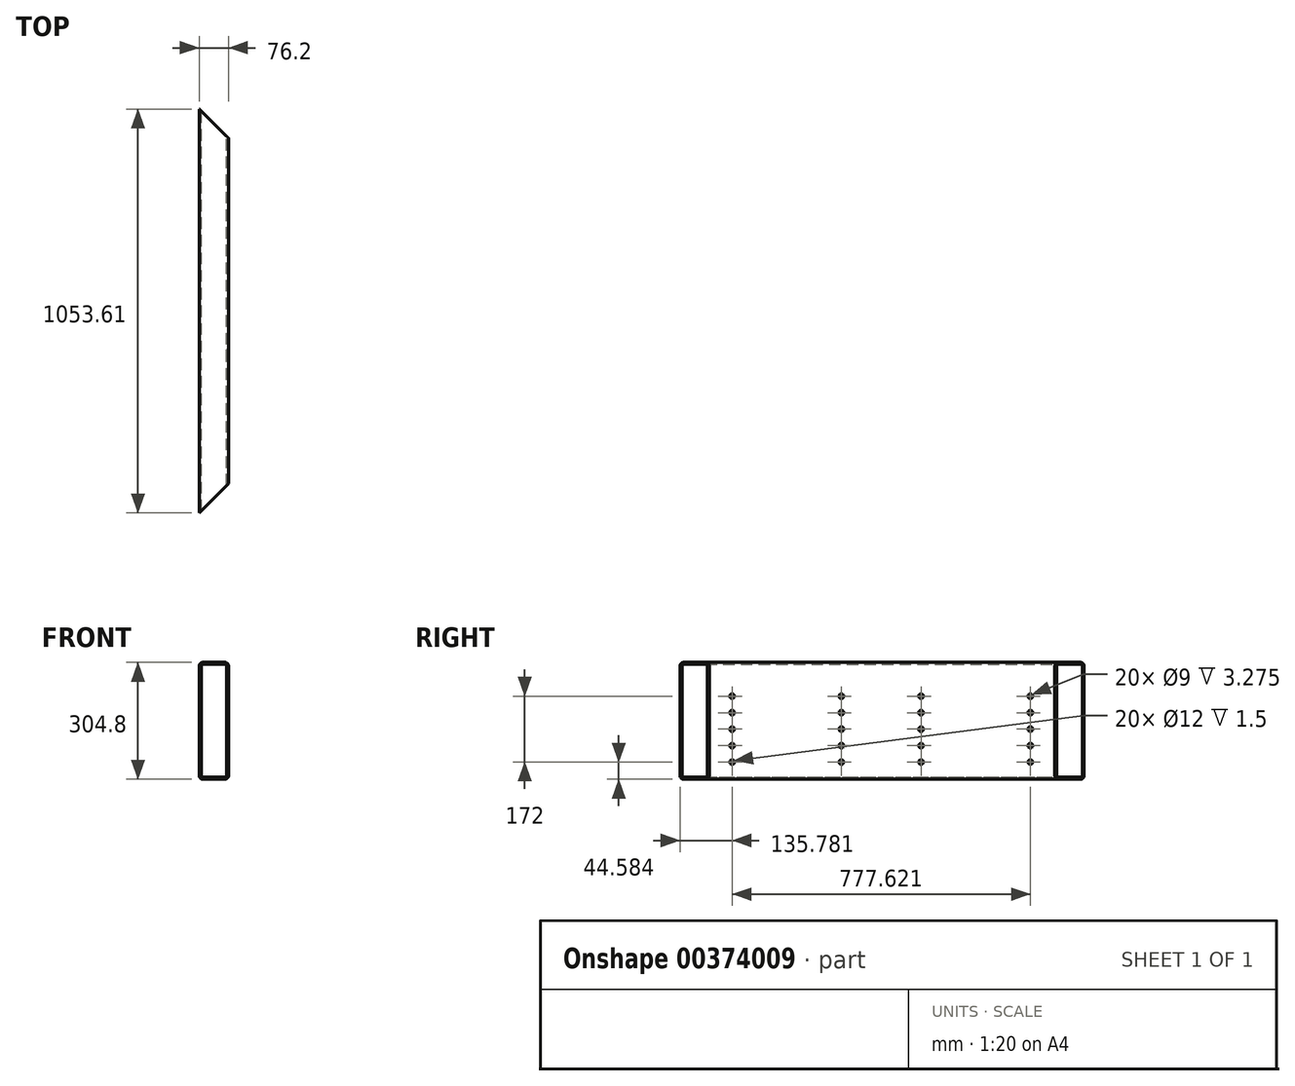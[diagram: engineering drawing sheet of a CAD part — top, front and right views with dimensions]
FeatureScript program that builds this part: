
annotation { "Feature Type Name" : "Feature", "Feature Type Description" : "" }
export const myFeature = defineFeature(function(context is Context, id is Id, definition is map)
    precondition{}
    {
        {
            var Q0;
            Q0=qCreatedBy(makeId("Front.planeOp"),FACE);
            var sketch = newSketch(context, id + "F0", { "sketchPlane" : qUnion([Q0])});
            skLineSegment(sketch, "E0.bottom", {"start": v(-9.55, -50.8) * mm, "end": v(-66.65, -50.8) * mm});
            skLineSegment(sketch, "E0.top", {"start": v(-9.55, 254) * mm, "end": v(-66.65, 254) * mm});
            skLineSegment(sketch, "E0.left", {"start": v(0, -41.25) * mm, "end": v(0, 244.45) * mm});
            skLineSegment(sketch, "E0.right", {"start": v(-76.2, -41.25) * mm, "end": v(-76.2, 244.45) * mm});
            skLineSegment(sketch, "E1.bottom", {"start": v(-66.65, 249.22) * mm, "end": v(-9.55, 249.22) * mm});
            skLineSegment(sketch, "E1.top", {"start": v(-66.65, -46.02) * mm, "end": v(-9.55, -46.02) * mm});
            skLineSegment(sketch, "E1.left", {"start": v(-71.42, 244.45) * mm, "end": v(-71.42, -41.25) * mm});
            skLineSegment(sketch, "E1.right", {"start": v(-4.78, 244.45) * mm, "end": v(-4.78, -41.25) * mm});
            skPoint(sketch, "E2.visualSharp", {"position": v(-71.42, 249.22) * mm});
            skArc(sketch, "E2.filletArc", {"start": v(-66.65, 249.22) * mm, "mid": v(-70.03, 247.83) * mm, "end": v(-71.42, 244.45) * mm});
            skPoint(sketch, "E3.visualSharp", {"position": v(-4.78, 249.22) * mm});
            skArc(sketch, "E3.filletArc", {"start": v(-4.78, 244.45) * mm, "mid": v(-6.17, 247.83) * mm, "end": v(-9.55, 249.22) * mm});
            skPoint(sketch, "E4.visualSharp", {"position": v(-4.78, -46.02) * mm});
            skArc(sketch, "E4.filletArc", {"start": v(-9.55, -46.02) * mm, "mid": v(-6.17, -44.63) * mm, "end": v(-4.78, -41.25) * mm});
            skPoint(sketch, "E5.visualSharp", {"position": v(-71.42, -46.02) * mm});
            skArc(sketch, "E5.filletArc", {"start": v(-71.42, -41.25) * mm, "mid": v(-70.03, -44.63) * mm, "end": v(-66.65, -46.02) * mm});
            skPoint(sketch, "E6.visualSharp", {"position": v(-76.2, 254) * mm});
            skArc(sketch, "E6.filletArc", {"start": v(-66.65, 254) * mm, "mid": v(-73.4, 251.2) * mm, "end": v(-76.2, 244.45) * mm});
            skPoint(sketch, "E7.visualSharp", {"position": v(0, 254) * mm});
            skArc(sketch, "E7.filletArc", {"start": v(0, 244.45) * mm, "mid": v(-2.8, 251.2) * mm, "end": v(-9.55, 254) * mm});
            skPoint(sketch, "E8.visualSharp", {"position": v(0, 0) * mm});
            skArc(sketch, "E8.filletArc", {"start": v(-9.55, -50.8) * mm, "mid": v(-2.8, -48) * mm, "end": v(0, -41.25) * mm});
            skPoint(sketch, "E9.visualSharp", {"position": v(-76.2, -50.8) * mm});
            skArc(sketch, "E9.filletArc", {"start": v(-76.2, -41.25) * mm, "mid": v(-73.4, -48) * mm, "end": v(-66.65, -50.8) * mm});
            skSolve(sketch);
        }
        {
            var Q0;
            Q0=qSketchRegion(id+"F0",true);
            extrude(context, id + "F1", {"entities" : qUnion([Q0]), "offsetDistance" : 25 * mm, "depth" : 1121.5 * mm});
        }
        {
            var Q0;
            Q0=makeQuery(id+"F1.opExtrude","SWEPT_FACE",FACE,{"disambiguationData":[OSD([sQuery(id+"F0.wireOp",EDGE,"E0.top")])]});
            var sketch = newSketch(context, id + "F2", { "sketchPlane" : qUnion([Q0])});
            skLineSegment(sketch, "E10", {"start": v(-76.2, 0) * mm, "end": v(0, -76.2) * mm});
            skLineSegment(sketch, "E11", {"start": v(0, -76.2) * mm, "end": v(0, 0) * mm});
            skLineSegment(sketch, "E12", {"start": v(0, 0) * mm, "end": v(-76.2, 0) * mm});
            skLineSegment(sketch, "E13", {"start": v(-76.2, -1121.5) * mm, "end": v(0, -1045.3) * mm});
            skLineSegment(sketch, "E14", {"start": v(0, -1045.3) * mm, "end": v(0, -1121.5) * mm});
            skLineSegment(sketch, "E15", {"start": v(0, -1121.5) * mm, "end": v(-76.2, -1121.5) * mm});
            skSolve(sketch);
        }
        {
            var Q0;
            Q0 = qSketchRegion(id + "F2", true);
            extrude(context, id + "F3", {"entities" : qUnion([Q0]), "operationType" : NewBodyOperationType.REMOVE, "endBound" : BoundingType.THROUGH_ALL, "oppositeDirection" : true, "depth" : 25.4 * mm});
        }
        {
            var Q0;
            Q0=makeQuery(id+"F1.opExtrude","SWEPT_BODY",BODY,{"disambiguationData":[OSD([sQuery(id+"F0.wireOp",EDGE,"E0.bottom"),sQuery(id+"F0.wireOp",EDGE,"E0.top"),sQuery(id+"F0.wireOp",EDGE,"E0.left"),sQuery(id+"F0.wireOp",EDGE,"E0.right"),sQuery(id+"F0.wireOp",EDGE,"E1.bottom"),sQuery(id+"F0.wireOp",EDGE,"E1.top"),sQuery(id+"F0.wireOp",EDGE,"E1.left"),sQuery(id+"F0.wireOp",EDGE,"E1.right"),sQuery(id+"F0.wireOp",EDGE,"E2.filletArc"),sQuery(id+"F0.wireOp",EDGE,"E3.filletArc"),sQuery(id+"F0.wireOp",EDGE,"E4.filletArc"),sQuery(id+"F0.wireOp",EDGE,"E5.filletArc"),sQuery(id+"F0.wireOp",EDGE,"E6.filletArc"),sQuery(id+"F0.wireOp",EDGE,"E7.filletArc"),sQuery(id+"F0.wireOp",EDGE,"E8.filletArc"),sQuery(id+"F0.wireOp",EDGE,"E9.filletArc")])]});
            transform(context, id + "F4", {"entities" : qUnion([Q0]), "transformType" : TransformType.TRANSLATION_3D, "dx" : 0 * mm, "dy" : 25.4 * mm, "dz" : 0 * mm, "makeCopy" : false});
        }
        {
            var Q0;
            Q0=makeQuery(id+"F1.opExtrude","SWEPT_FACE",FACE,{"disambiguationData":[OSD([sQuery(id+"F0.wireOp",EDGE,"E0.left")])]});
            var sketch = newSketch(context, id + "F5", { "sketchPlane" : qUnion([Q0])});
            skPoint(sketch, "E16", {"position": v(-114.8, 165.78) * mm});
            skPoint(sketch, "E17", {"position": v(-399.85, 165.78) * mm});
            skPoint(sketch, "E18", {"position": v(-607.4, 165.78) * mm});
            skPoint(sketch, "E19", {"position": v(-892.43, 165.78) * mm});
            skPoint(sketch, "E20", {"position": v(-892.43, 122.78) * mm});
            skPoint(sketch, "E21", {"position": v(-892.43, 79.78) * mm});
            skPoint(sketch, "E22", {"position": v(-892.43, 36.78) * mm});
            skPoint(sketch, "E23", {"position": v(-892.43, -6.22) * mm});
            skPoint(sketch, "E24", {"position": v(-607.4, 122.78) * mm});
            skPoint(sketch, "E25", {"position": v(-607.4, 79.78) * mm});
            skPoint(sketch, "E26", {"position": v(-607.4, 36.78) * mm});
            skPoint(sketch, "E27", {"position": v(-607.4, -6.22) * mm});
            skPoint(sketch, "E28", {"position": v(-399.85, 122.78) * mm});
            skPoint(sketch, "E29", {"position": v(-399.85, 79.78) * mm});
            skPoint(sketch, "E30", {"position": v(-399.85, 36.78) * mm});
            skPoint(sketch, "E31", {"position": v(-399.85, -6.22) * mm});
            skPoint(sketch, "E32", {"position": v(-114.8, 122.78) * mm});
            skPoint(sketch, "E33", {"position": v(-114.8, 79.78) * mm});
            skPoint(sketch, "E34", {"position": v(-114.8, 36.78) * mm});
            skPoint(sketch, "E35", {"position": v(-114.8, -6.22) * mm});
            skLineSegment(sketch, "E36", {"start": v(-892.43, 165.78) * mm, "end": v(-114.8, 165.78) * mm, "construction": true});
            skLineSegment(sketch, "E37", {"start": v(-892.43, 122.78) * mm, "end": v(-114.8, 122.78) * mm, "construction": true});
            skLineSegment(sketch, "E38", {"start": v(-892.43, 79.78) * mm, "end": v(-114.8, 79.78) * mm, "construction": true});
            skLineSegment(sketch, "E39", {"start": v(-892.43, 36.78) * mm, "end": v(-114.8, 36.78) * mm, "construction": true});
            skLineSegment(sketch, "E40", {"start": v(-892.43, -6.22) * mm, "end": v(-114.8, -6.22) * mm, "construction": true});
            skLineSegment(sketch, "E41", {"start": v(-114.8, 165.78) * mm, "end": v(-114.8, -6.22) * mm, "construction": true});
            skLineSegment(sketch, "E42", {"start": v(-399.85, 165.78) * mm, "end": v(-399.85, -6.22) * mm, "construction": true});
            skLineSegment(sketch, "E43", {"start": v(-607.4, 165.78) * mm, "end": v(-607.4, -6.22) * mm, "construction": true});
            skLineSegment(sketch, "E44", {"start": v(-892.43, 165.78) * mm, "end": v(-892.43, -6.22) * mm, "construction": true});
            skSolve(sketch);
        }
        {
            var Q0;
            Q0=sQuery(id+"F5.wireOp",VERTEX,"E19");
            var Q1;
            Q1=sQuery(id+"F5.wireOp",VERTEX,"E20");
            var Q2;
            Q2=sQuery(id+"F5.wireOp",VERTEX,"E21");
            var Q3;
            Q3=sQuery(id+"F5.wireOp",VERTEX,"E22");
            var Q4;
            Q4=sQuery(id+"F5.wireOp",VERTEX,"E23");
            var Q5;
            Q5=sQuery(id+"F5.wireOp",VERTEX,"E18");
            var Q6;
            Q6=sQuery(id+"F5.wireOp",VERTEX,"E24");
            var Q7;
            Q7=sQuery(id+"F5.wireOp",VERTEX,"E25");
            var Q8;
            Q8=sQuery(id+"F5.wireOp",VERTEX,"E26");
            var Q9;
            Q9=sQuery(id+"F5.wireOp",VERTEX,"E27");
            var Q10;
            Q10=sQuery(id+"F5.wireOp",VERTEX,"E17");
            var Q11;
            Q11=sQuery(id+"F5.wireOp",VERTEX,"E28");
            var Q12;
            Q12=sQuery(id+"F5.wireOp",VERTEX,"E29");
            var Q13;
            Q13=sQuery(id+"F5.wireOp",VERTEX,"E30");
            var Q14;
            Q14=sQuery(id+"F5.wireOp",VERTEX,"E31");
            var Q15;
            Q15=sQuery(id+"F5.wireOp",VERTEX,"E16");
            var Q16;
            Q16=sQuery(id+"F5.wireOp",VERTEX,"E32");
            var Q17;
            Q17=sQuery(id+"F5.wireOp",VERTEX,"E33");
            var Q18;
            Q18=sQuery(id+"F5.wireOp",VERTEX,"E34");
            var Q19;
            Q19=sQuery(id+"F5.wireOp",VERTEX,"E35");
            var Q20;
            Q20=makeQuery(id+"F1.opExtrude","SWEPT_BODY",BODY,{"disambiguationData":[OSD([sQuery(id+"F0.wireOp",EDGE,"E0.bottom"),sQuery(id+"F0.wireOp",EDGE,"E0.top"),sQuery(id+"F0.wireOp",EDGE,"E0.left"),sQuery(id+"F0.wireOp",EDGE,"E0.right"),sQuery(id+"F0.wireOp",EDGE,"E1.bottom"),sQuery(id+"F0.wireOp",EDGE,"E1.top"),sQuery(id+"F0.wireOp",EDGE,"E1.left"),sQuery(id+"F0.wireOp",EDGE,"E1.right"),sQuery(id+"F0.wireOp",EDGE,"E2.filletArc"),sQuery(id+"F0.wireOp",EDGE,"E3.filletArc"),sQuery(id+"F0.wireOp",EDGE,"E4.filletArc"),sQuery(id+"F0.wireOp",EDGE,"E5.filletArc"),sQuery(id+"F0.wireOp",EDGE,"E6.filletArc"),sQuery(id+"F0.wireOp",EDGE,"E7.filletArc"),sQuery(id+"F0.wireOp",EDGE,"E8.filletArc"),sQuery(id+"F0.wireOp",EDGE,"E9.filletArc")])]});
            hole(context, id + "F6", {"style" : HoleStyle.C_BORE, "endStyle" : HoleEndStyle.BLIND, "holeDiameter" : 9 * mm, "cBoreDiameter" : 12 * mm, "cBoreDepth" : 1.5 * mm, "majorDiameter" : 5 * mm, "holeDepth" : 10 * mm, "isTappedThrough" : true, "tappedDepth" : 17 * mm, "tapClearance" : 3, "locations" : qUnion([Q0, Q1, Q2, Q3, Q4, Q5, Q6, Q7, Q8, Q9, Q10, Q11, Q12, Q13, Q14, Q15, Q16, Q17, Q18, Q19]), "scope" : qUnion([Q20]), "startStyle" : HoleStartStyle.SKETCH});
        }
        {
            var Q0;
            Q0=makeQuery(id+"F1.opExtrude","SWEPT_FACE",FACE,{"disambiguationData":[OSD([sQuery(id+"F0.wireOp",EDGE,"E0.top")])]});
            var sketch = newSketch(context, id + "F7", { "sketchPlane" : qUnion([Q0])});
            skLineSegment(sketch, "E45", {"start": v(-76.2, -1028.2) * mm, "end": v(0, -952) * mm});
            skLineSegment(sketch, "E46", {"start": v(0, -952) * mm, "end": v(0, -1096.1) * mm});
            skLineSegment(sketch, "E47", {"start": v(0, -1096.1) * mm, "end": v(-76.2, -1096.1) * mm});
            skLineSegment(sketch, "E48", {"start": v(-76.2, -1096.1) * mm, "end": v(-76.2, -1028.2) * mm});
            skSolve(sketch);
        }
        {
            var Q0;
            Q0 = qSketchRegion(id + "F7", true);
            var Q1;
            Q1=makeQuery(id+"F1.opExtrude","SWEPT_FACE",FACE,{"disambiguationData":[OSD([sQuery(id+"F0.wireOp",EDGE,"E0.bottom")])]});
            extrude(context, id + "F8", {"entities" : qUnion([Q0]), "operationType" : NewBodyOperationType.REMOVE, "endBound" : BoundingType.UP_TO_SURFACE, "oppositeDirection" : true, "depth" : 25 * mm, "endBoundEntityFace" : qUnion([Q1]), "offsetDistance" : 25 * mm});
        }
    });
